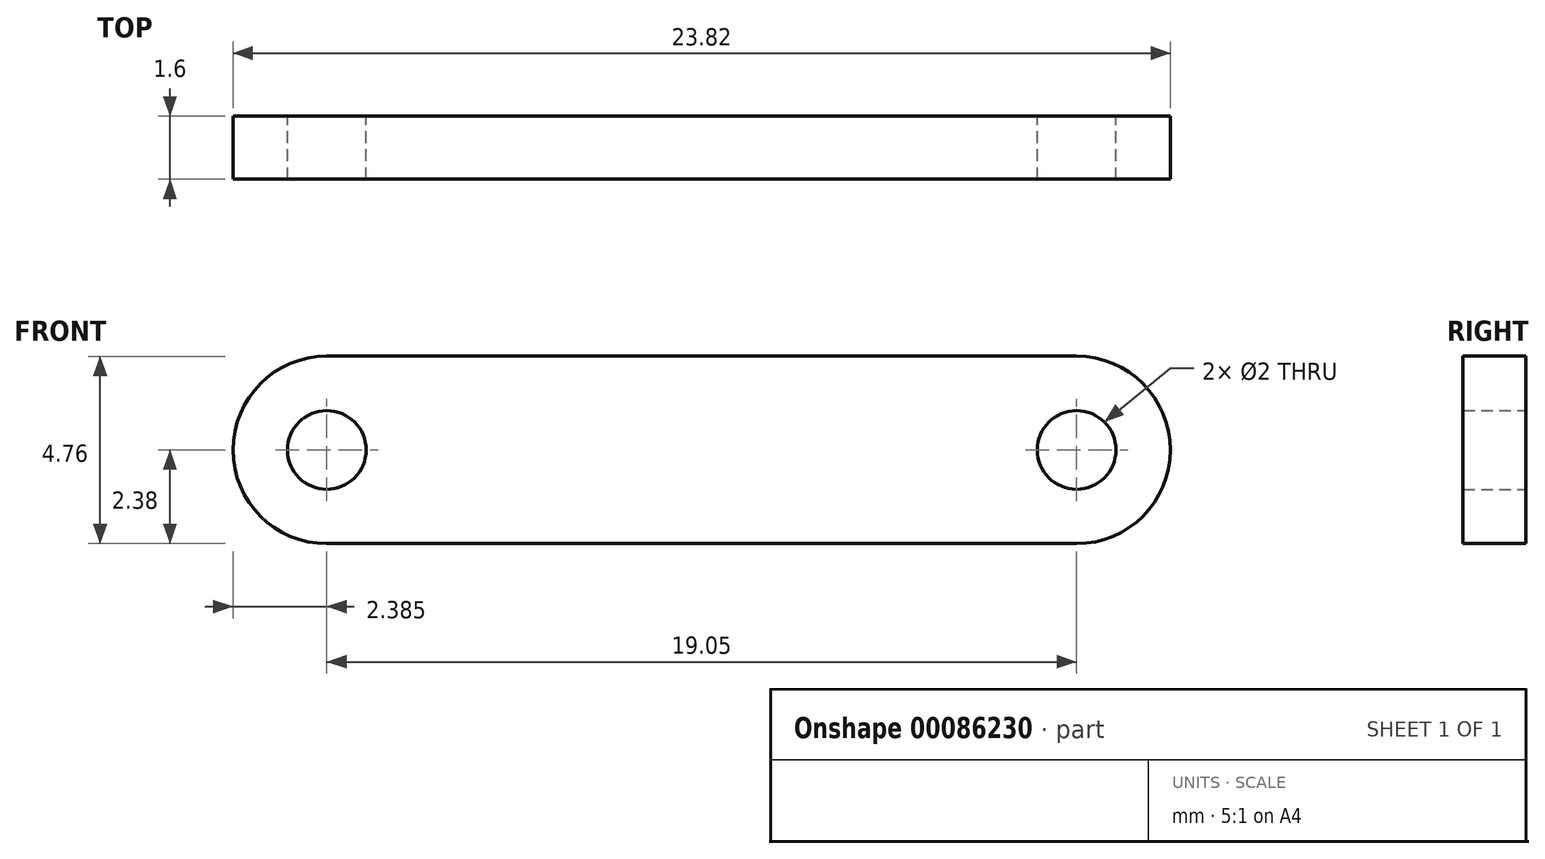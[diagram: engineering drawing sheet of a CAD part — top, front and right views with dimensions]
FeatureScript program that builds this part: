
annotation { "Feature Type Name" : "Feature", "Feature Type Description" : "" }
export const myFeature = defineFeature(function(context is Context, id is Id, definition is map)
    precondition{}
    {
        {
            var Q0;
            Q0=qCreatedBy(makeId("Front.planeOp"),FACE);
            var sketch = newSketch(context, id + "F0", { "sketchPlane" : qUnion([Q0])});
            skLineSegment(sketch, "E0.bottom", {"start": v(-9.52, 2.38) * mm, "end": v(9.53, 2.38) * mm});
            skLineSegment(sketch, "E0.top", {"start": v(-9.52, -2.38) * mm, "end": v(9.53, -2.38) * mm});
            skPoint(sketch, "E0.middle", {"position": v(0, 0) * mm});
            skArc(sketch, "E1", {"start": v(-9.52, 2.38) * mm, "mid": v(-11.9, 0) * mm, "end": v(-9.52, -2.38) * mm});
            skArc(sketch, "E2", {"start": v(9.53, -2.38) * mm, "mid": v(11.9, 0) * mm, "end": v(9.53, 2.38) * mm});
            skLineSegment(sketch, "E3", {"start": v(-9.52, 0) * mm, "end": v(0, 0) * mm, "construction": true});
            skLineSegment(sketch, "E4", {"start": v(9.53, 0) * mm, "end": v(0, 0) * mm, "construction": true});
            skCircle(sketch, "E5", {"center": v(9.53, 0) * mm, "radius": 1 * mm});
            skCircle(sketch, "E6", {"center": v(-9.52, 0) * mm, "radius": 1 * mm});
            skSolve(sketch);
        }
        {
            var Q0;
            Q0=makeQuery(id+"F0.imprint","IMPRINT",FACE,{"disambiguationData":[TD([[makeQuery(id+"F0.imprint","IMPRINT",EDGE,{"derivedFrom":sQuery(id+"F0.wireOp",EDGE,"E0.bottom")}),-1.0]])]});
            extrude(context, id + "F1", {"entities" : qUnion([Q0]), "depth" : 1.6 * mm, "offsetDistance" : 25 * mm, "symmetric" : true});
        }
    });
